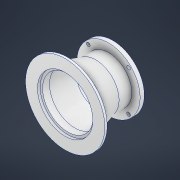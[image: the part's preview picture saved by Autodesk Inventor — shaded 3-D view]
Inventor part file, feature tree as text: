
AUTODESK INVENTOR PART (.ipt)
format: ipt  version: 2022 (Build 260153000, 153)  size: 179,200 bytes
history: native  units: mm
features: sketch x2, revolve x1, hole x1
ambient origin geometry x8: Origin, YZ Plane, XZ Plane, XY Plane, X Axis, Y Axis, Z Axis, Center Point
bodies: Solid1 (feature_tree)
feature tree (4):
  revolve  "Revolution1"  [1 undecoded]
  hole  "Hole1"  [1 undecoded]
  sketch  "Sketch1"  dims[d0=40.0mm d1=2.0mm]
  sketch  "Sketch2"  dims[d2=2.0mm d4=59.8mm d5=4.0mm d7=12.0mm d8=4.0mm d9=75.0mm d10=2.233mm d11=52.3mm d12=47.8mm d13=59.325mm d14=5.1mm d15=2.5mm d16=4.0mm d17=45.0mm d18=90.0deg d19=54.0mm d20=3.4mm d21=6.0mm d22=6.3mm d23=2.0mm d24=90.0deg d25=8.0mm d26=20.594885mm]
note: 2 required parameter values undecoded (feature->parameter linkage not recoverable at this tier; creation-order binding heuristic only, values carry confidence <= 0.55)